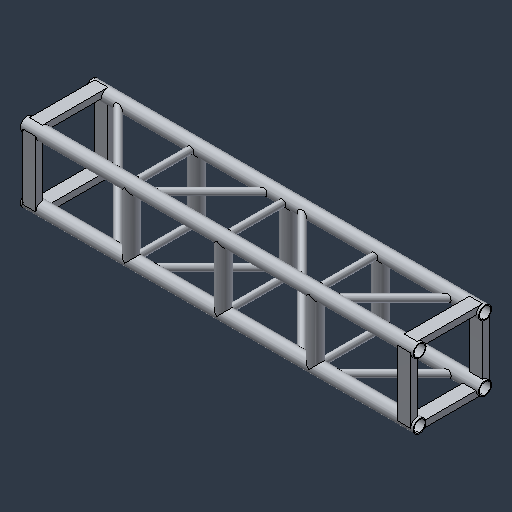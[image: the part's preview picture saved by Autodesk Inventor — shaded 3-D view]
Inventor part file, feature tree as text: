
AUTODESK INVENTOR PART (.ipt)
format: ipt  version: 2024.3 (Build 283343000, 343)  size: 323,072 bytes
history: native  units: mm (DEFAULTED — no unit token found)
features: imported_body x27, other x3, mirror x3
ambient origin geometry x8: Origin, YZ Plane, XZ Plane, XY Plane, X Axis, Y Axis, Z Axis, Center Point
bodies: Solid1 (feature_tree), Solid2 (feature_tree), Solid3 (feature_tree), Solid4 (feature_tree), Solid5 (feature_tree), Solid6 (feature_tree), Solid7 (feature_tree), Solid8 (feature_tree), Solid9 (feature_tree), Solid10 (feature_tree), Solid11 (feature_tree), Solid12 (feature_tree), Solid13 (feature_tree), Solid14 (feature_tree), Solid15 (feature_tree), Solid16 (feature_tree), Solid17 (feature_tree), Solid18 (feature_tree), Solid19 (feature_tree), Solid20 (feature_tree), Solid21 (feature_tree), Solid22 (feature_tree), Solid23 (feature_tree), Solid24 (feature_tree), Solid25 (feature_tree), Solid26 (feature_tree), Solid27 (feature_tree), Solid28 (feature_tree), Solid29 (feature_tree), Solid30 (feature_tree), Solid31 (feature_tree), Solid32 (feature_tree), Solid33 (feature_tree)
feature tree (33):
  imported_body  "Imported1"
  imported_body  "Imported2"
  imported_body  "Imported3"
  imported_body  "Imported4"
  imported_body  "Imported5"
  imported_body  "Imported6"
  imported_body  "Imported7"
  imported_body  "Imported8"
  imported_body  "Imported9"
  imported_body  "Imported10"
  imported_body  "Imported11"
  imported_body  "Imported12"
  imported_body  "Imported13"
  imported_body  "Imported14"
  imported_body  "Imported15"
  imported_body  "Imported16"
  imported_body  "Imported17"
  imported_body  "Imported18"
  imported_body  "Imported19"
  imported_body  "Imported20"
  imported_body  "Imported21"
  imported_body  "Imported22"
  imported_body  "Imported23"
  imported_body  "Imported24"
  imported_body  "Imported25"
  imported_body  "Imported26"
  imported_body  "Imported27"
  other  "Cut-Extrude1[1]"
  other  "Cut-Extrude1[2]"
  other  "Cut-Extrude1[3]"
  mirror  "Mirror1[1]"
  mirror  "Mirror1[2]"
  mirror  "Mirror1[3]"
